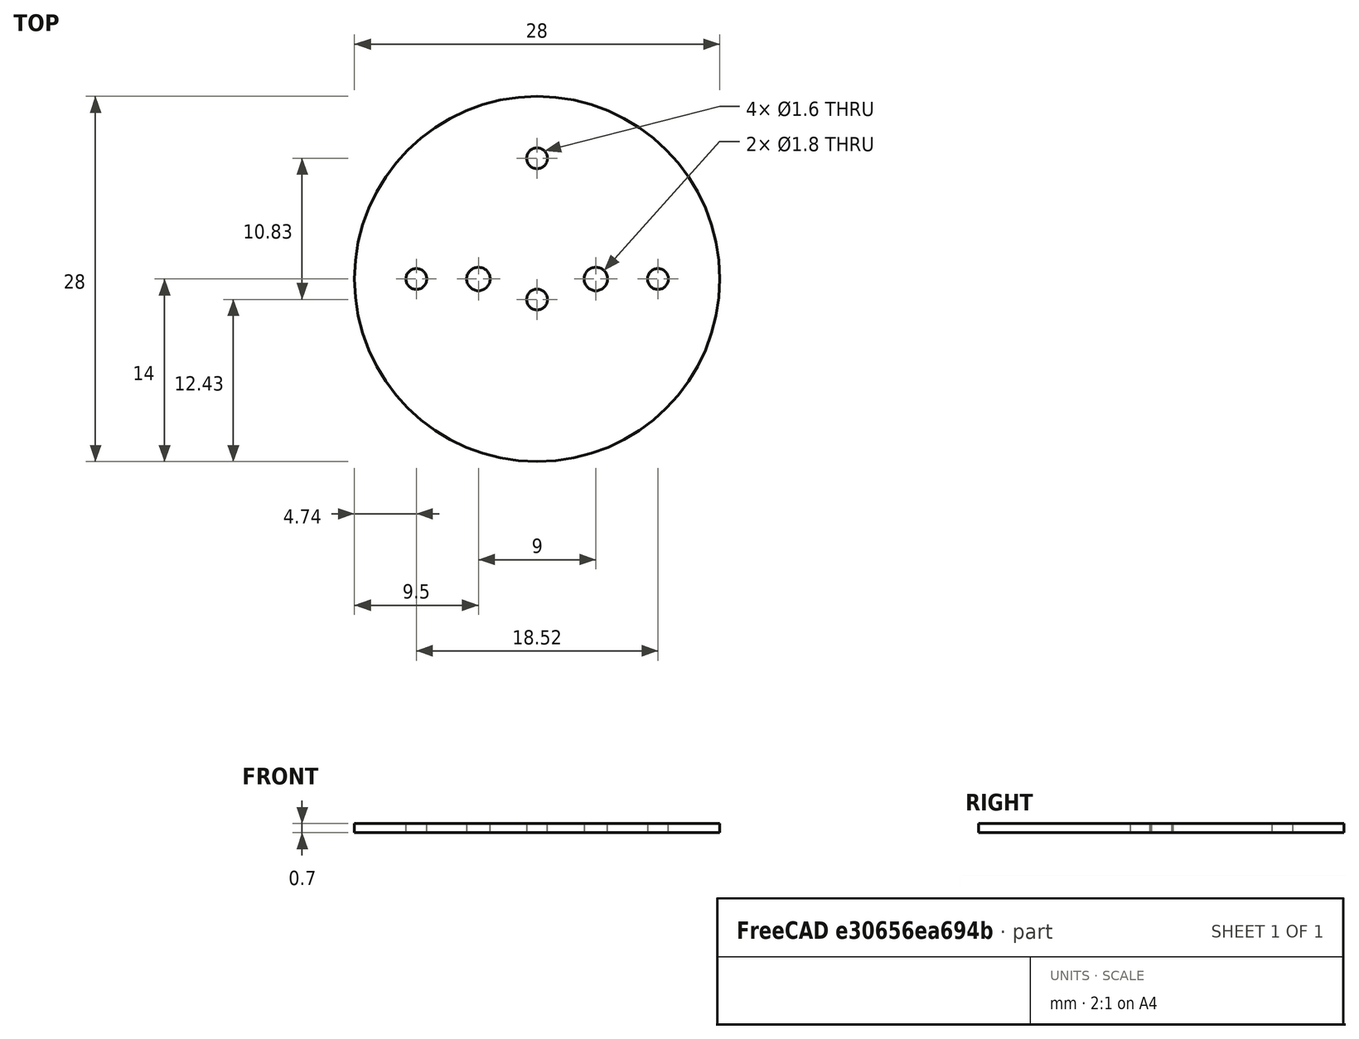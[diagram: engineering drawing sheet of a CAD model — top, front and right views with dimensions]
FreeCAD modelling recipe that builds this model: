
FCSTD DOCUMENT  (FreeCAD 0.16R)
Label: button_spacer
License: All rights reserved
LicenseURL: http://en.wikipedia.org/wiki/All_rights_reserved
objects: App::DocumentObjectGroup×1, Sketcher::SketchObject×1, PartDesign::Pad×1
note: 3 computed .brp shape members not serialized (recipe doc carries the construction recipe); baked Part::Feature solids carry a one-line shape summary decoded from their .brp

FEATURE [App::DocumentObjectGroup] Group
FEATURE [Sketcher::SketchObject] Sketch
  sketch-geometry (7):
    g0: Circle CenterX=4.5 CenterY=0 CenterZ=0 NormalX=0 NormalY=0 NormalZ=1 Radius=0.9
    g1: Circle CenterX=-4.5 CenterY=0 CenterZ=0 NormalX=0 NormalY=0 NormalZ=1 Radius=0.9
    g2: Circle CenterX=0 CenterY=-1.57 CenterZ=0 NormalX=0 NormalY=0 NormalZ=1 Radius=0.8
    g3: Circle CenterX=-9.26 CenterY=0 CenterZ=0 NormalX=0 NormalY=0 NormalZ=1 Radius=0.8
    g4: Circle CenterX=9.26 CenterY=0 CenterZ=0 NormalX=0 NormalY=0 NormalZ=1 Radius=0.8
    g5: Circle CenterX=0 CenterY=9.26 CenterZ=0 NormalX=0 NormalY=0 NormalZ=1 Radius=0.8
    g6: Circle CenterX=0 CenterY=0 CenterZ=0 NormalX=0 NormalY=0 NormalZ=1 Radius=14
  constraints (20):
    c: PointOnObject(g0,g-1)
    c: PointOnObject(g1,g-1)
    c: Radius(g1) = 0.9
    c: Equal(g1,g0)
    c: DistanceX(g1) = -4.5
    c: DistanceX(g0) = 4.5
    c: PointOnObject(g2,g-2)
    c: PointOnObject(g3,g-1)
    c: PointOnObject(g4,g-1)
    c: PointOnObject(g5,g-2)
    c: Coincident(g6,g-1)
    c: DistanceY(g2) = -1.57
    c: DistanceX(g3) = -9.26
    c: DistanceX(g4) = 9.26
    c: DistanceY(g5) = 9.26
    c: Radius(g6) = 14
    c: Radius(g3) = 0.8
    c: Equal(g3,g4)
    c: Equal(g3,g2)
    c: Equal(g3,g5)
FEATURE [PartDesign::Pad] Pad
  Length = 0.7
  Length2 = 100
  Sketch = -> Sketch
  Type = 0
